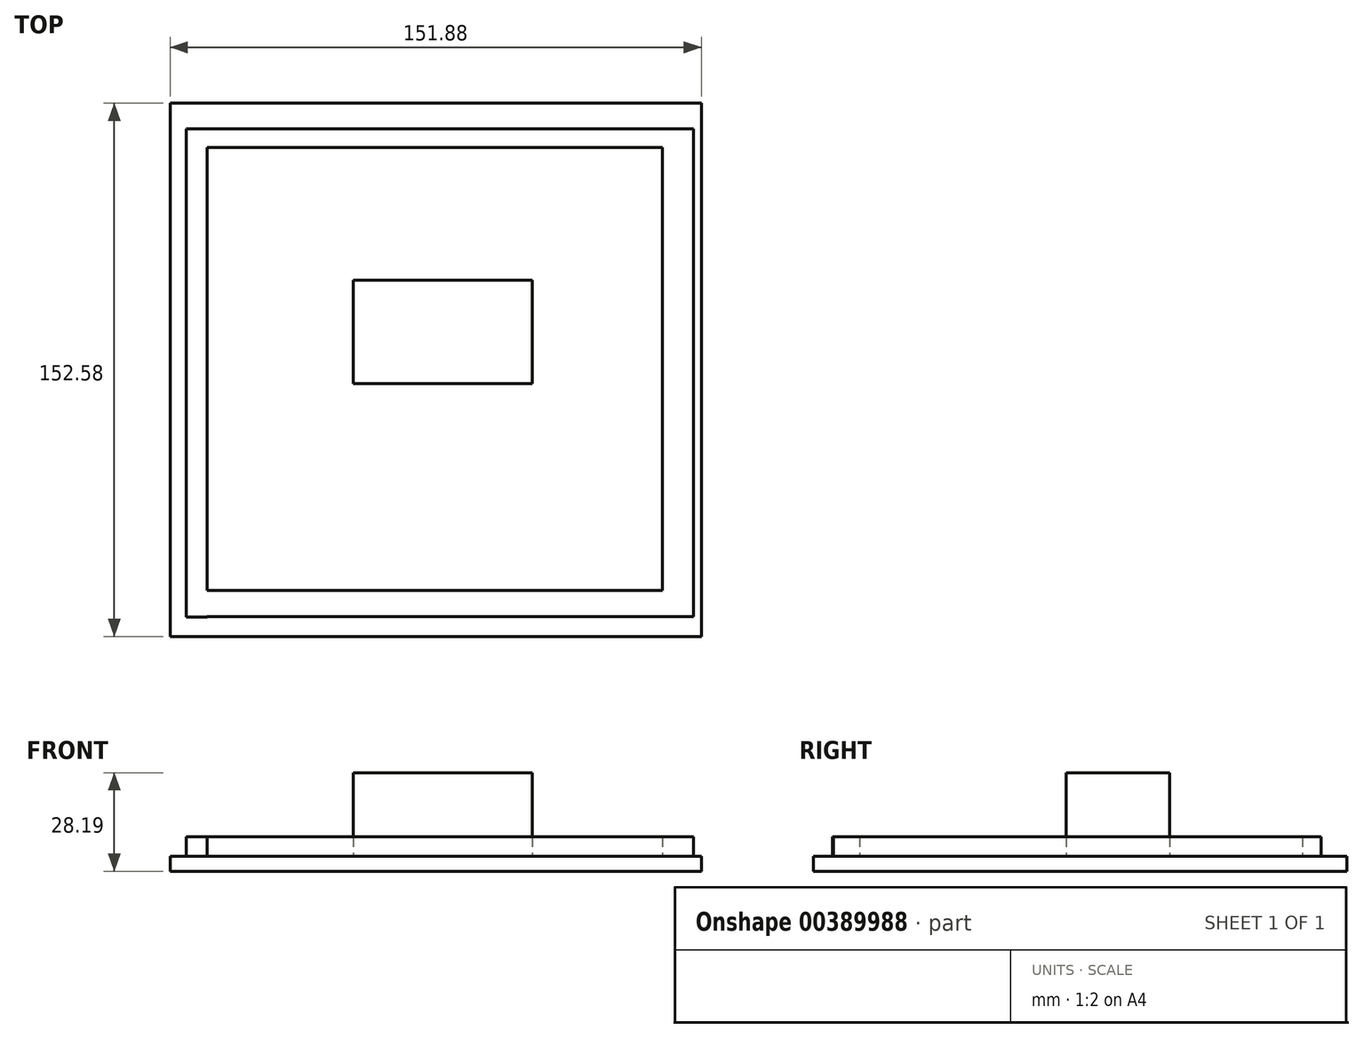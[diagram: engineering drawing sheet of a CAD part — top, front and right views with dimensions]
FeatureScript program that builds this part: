
annotation { "Feature Type Name" : "Feature", "Feature Type Description" : "" }
export const myFeature = defineFeature(function(context is Context, id is Id, definition is map)
    precondition{}
    {
        {
            var Q0;
            Q0=qCreatedBy(makeId("Top.planeOp"),FACE);
            var sketch = newSketch(context, id + "F0", { "sketchPlane" : qUnion([Q0])});
            skLineSegment(sketch, "E0.bottom", {"start": v(76.06, 76.29) * mm, "end": v(-75.82, 76.29) * mm});
            skLineSegment(sketch, "E0.top", {"start": v(76.06, -76.29) * mm, "end": v(-75.82, -76.29) * mm});
            skLineSegment(sketch, "E0.left", {"start": v(76.06, 76.29) * mm, "end": v(76.06, -76.29) * mm});
            skLineSegment(sketch, "E0.right", {"start": v(-75.82, 76.29) * mm, "end": v(-75.82, -76.29) * mm});
            skSolve(sketch);
        }
        {
            var Q0;
            Q0 = qSketchRegion(id + "F0", true);
            extrude(context, id + "F1", {"entities" : qUnion([Q0]), "depth" : 4.32 * mm});
        }
        {
            var Q0;
            Q0=makeQuery(id+"F1.opExtrude","CAP_FACE",FACE,{"disambiguationData":[OSD([sQuery(id+"F0.wireOp",EDGE,"E0.bottom"),sQuery(id+"F0.wireOp",EDGE,"E0.top"),sQuery(id+"F0.wireOp",EDGE,"E0.left"),sQuery(id+"F0.wireOp",EDGE,"E0.right")])],"isStart":false});
            var sketch = newSketch(context, id + "F2", { "sketchPlane" : qUnion([Q0])});
            skLineSegment(sketch, "E1.bottom", {"start": v(-65.2, 68.93) * mm, "end": v(-71.25, 68.93) * mm});
            skLineSegment(sketch, "E1.top", {"start": v(-65.2, -70.79) * mm, "end": v(-71.25, -70.79) * mm});
            skLineSegment(sketch, "E1.left", {"start": v(-65.2, 68.93) * mm, "end": v(-65.2, -70.79) * mm});
            skLineSegment(sketch, "E1.right", {"start": v(-71.25, 68.93) * mm, "end": v(-71.25, -70.79) * mm});
            skLineSegment(sketch, "E2.bottom", {"start": v(-65.2, 68.93) * mm, "end": v(64.97, 68.93) * mm});
            skLineSegment(sketch, "E2.top", {"start": v(-65.2, 63.57) * mm, "end": v(64.97, 63.57) * mm});
            skLineSegment(sketch, "E2.left", {"start": v(-65.2, 68.93) * mm, "end": v(-65.2, 63.57) * mm});
            skLineSegment(sketch, "E2.right", {"start": v(64.97, 68.93) * mm, "end": v(64.97, 63.57) * mm});
            skLineSegment(sketch, "E3.bottom", {"start": v(64.97, 68.93) * mm, "end": v(73.82, 68.93) * mm});
            skLineSegment(sketch, "E3.top", {"start": v(64.97, -70.56) * mm, "end": v(73.82, -70.56) * mm});
            skLineSegment(sketch, "E3.left", {"start": v(64.97, 68.93) * mm, "end": v(64.97, -70.56) * mm});
            skLineSegment(sketch, "E3.right", {"start": v(73.82, 68.93) * mm, "end": v(73.82, -70.56) * mm});
            skLineSegment(sketch, "E4.bottom", {"start": v(64.97, -70.56) * mm, "end": v(-65.2, -70.56) * mm});
            skLineSegment(sketch, "E4.top", {"start": v(64.97, -63.1) * mm, "end": v(-65.2, -63.1) * mm});
            skLineSegment(sketch, "E4.left", {"start": v(64.97, -70.56) * mm, "end": v(64.97, -63.1) * mm});
            skLineSegment(sketch, "E4.right", {"start": v(-65.2, -70.56) * mm, "end": v(-65.2, -63.1) * mm});
            skSolve(sketch);
        }
        {
            var Q0;
            Q0 = qSketchRegion(id + "F2", true);
            extrude(context, id + "F3", {"entities" : qUnion([Q0]), "operationType" : NewBodyOperationType.ADD, "depth" : 5.6 * mm});
        }
        {
            var Q0;
            {var subQ0=sQuery(id+"F2.wireOp",EDGE,"E2.top");Q0=makeQuery(id+"F3.boolean.opBoolean","SPLIT",FACE,{"disambiguationData":[TD([makeQuery(id+"F3.opExtrude","SWEPT_FACE",FACE,{"disambiguationData":[OSD([subQ0])]})])],"derivedFrom":makeQuery(id+"F1.opExtrude","CAP_FACE",FACE,{"disambiguationData":[OSD([sQuery(id+"F0.wireOp",EDGE,"E0.bottom"),sQuery(id+"F0.wireOp",EDGE,"E0.top"),sQuery(id+"F0.wireOp",EDGE,"E0.left"),sQuery(id+"F0.wireOp",EDGE,"E0.right")])],"isStart":false})});}
            var sketch = newSketch(context, id + "F4", { "sketchPlane" : qUnion([Q0])});
            skLineSegment(sketch, "E5.bottom", {"start": v(-23.52, 25.61) * mm, "end": v(27.71, 25.61) * mm});
            skLineSegment(sketch, "E5.top", {"start": v(-23.52, -3.96) * mm, "end": v(27.71, -3.96) * mm});
            skLineSegment(sketch, "E5.left", {"start": v(-23.52, 25.61) * mm, "end": v(-23.52, -3.96) * mm});
            skLineSegment(sketch, "E5.right", {"start": v(27.71, 25.61) * mm, "end": v(27.71, -3.96) * mm});
            skSolve(sketch);
        }
        {
            var Q0;
            Q0 = qSketchRegion(id + "F4", true);
            extrude(context, id + "F5", {"entities" : qUnion([Q0]), "operationType" : NewBodyOperationType.ADD, "depth" : 23.88 * mm});
        }
    });
